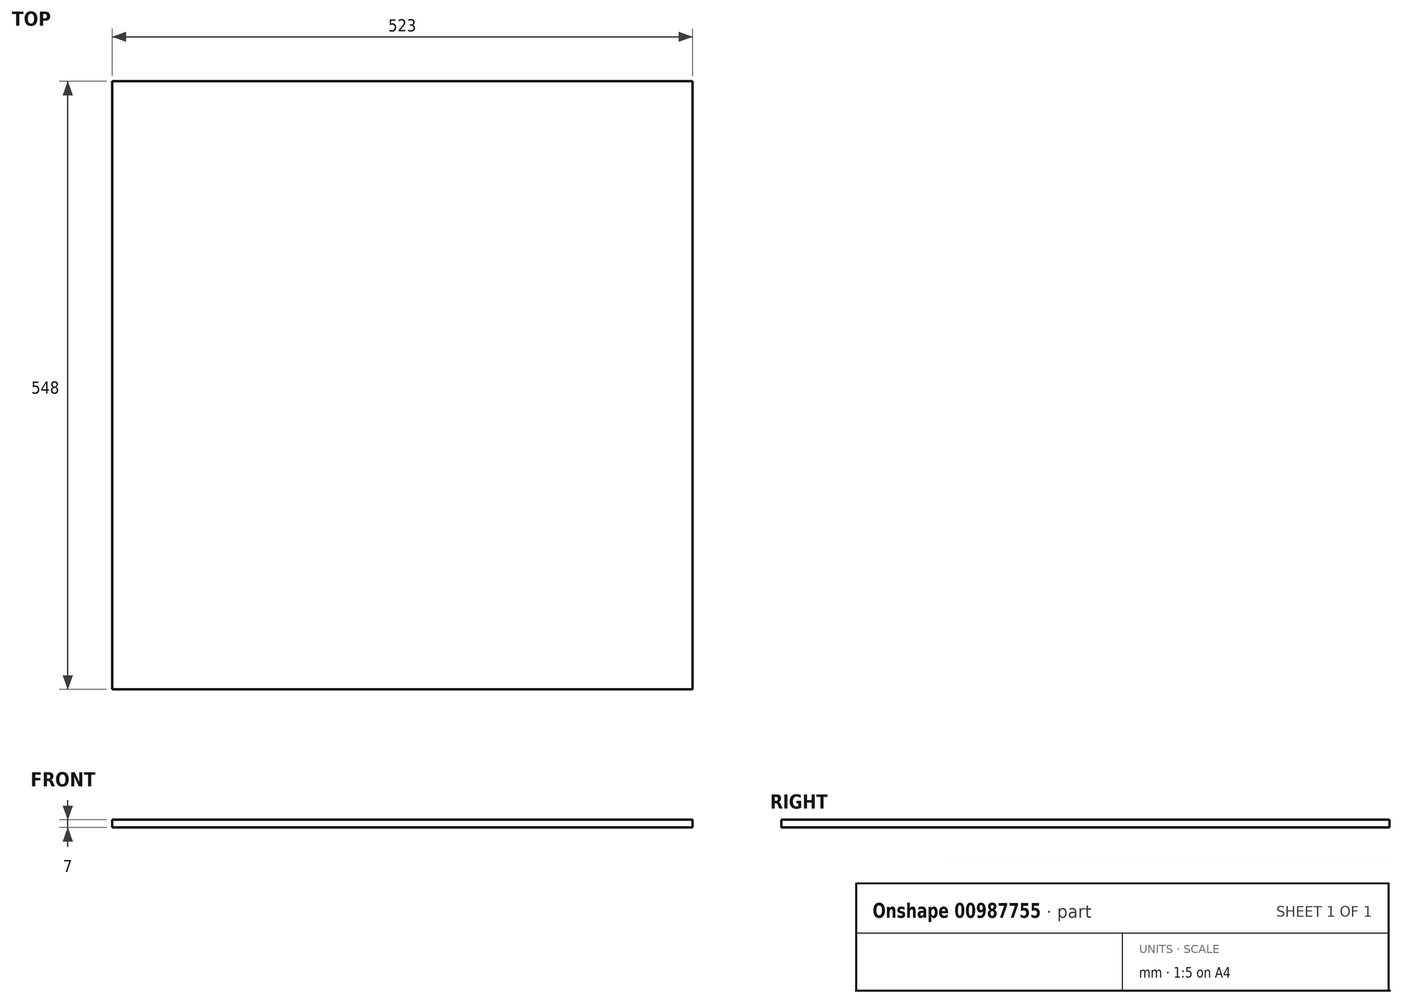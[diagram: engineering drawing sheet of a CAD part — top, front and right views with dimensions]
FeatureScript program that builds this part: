
annotation { "Feature Type Name" : "Feature", "Feature Type Description" : "" }
export const myFeature = defineFeature(function(context is Context, id is Id, definition is map)
    precondition{}
    {
        {
            var Q0;
            Q0=qCreatedBy(makeId("Top.planeOp"),FACE);
            var sketch = newSketch(context, id + "F0", { "sketchPlane" : qUnion([Q0])});
            skLineSegment(sketch, "E0.bottom", {"start": v(-261.5, 274) * mm, "end": v(261.5, 274) * mm});
            skLineSegment(sketch, "E0.top", {"start": v(-261.5, -274) * mm, "end": v(261.5, -274) * mm});
            skLineSegment(sketch, "E0.left", {"start": v(-261.5, 274) * mm, "end": v(-261.5, -274) * mm});
            skLineSegment(sketch, "E0.right", {"start": v(261.5, 274) * mm, "end": v(261.5, -274) * mm});
            skPoint(sketch, "E0.middle", {"position": v(0, 0) * mm});
            skSolve(sketch);
        }
        {
            var Q0;
            Q0 = qSketchRegion(id + "F0", true);
            extrude(context, id + "F1", {"entities" : qUnion([Q0]), "oppositeDirection" : true, "depth" : 7 * mm, "offsetDistance" : 25 * mm});
        }
    });
